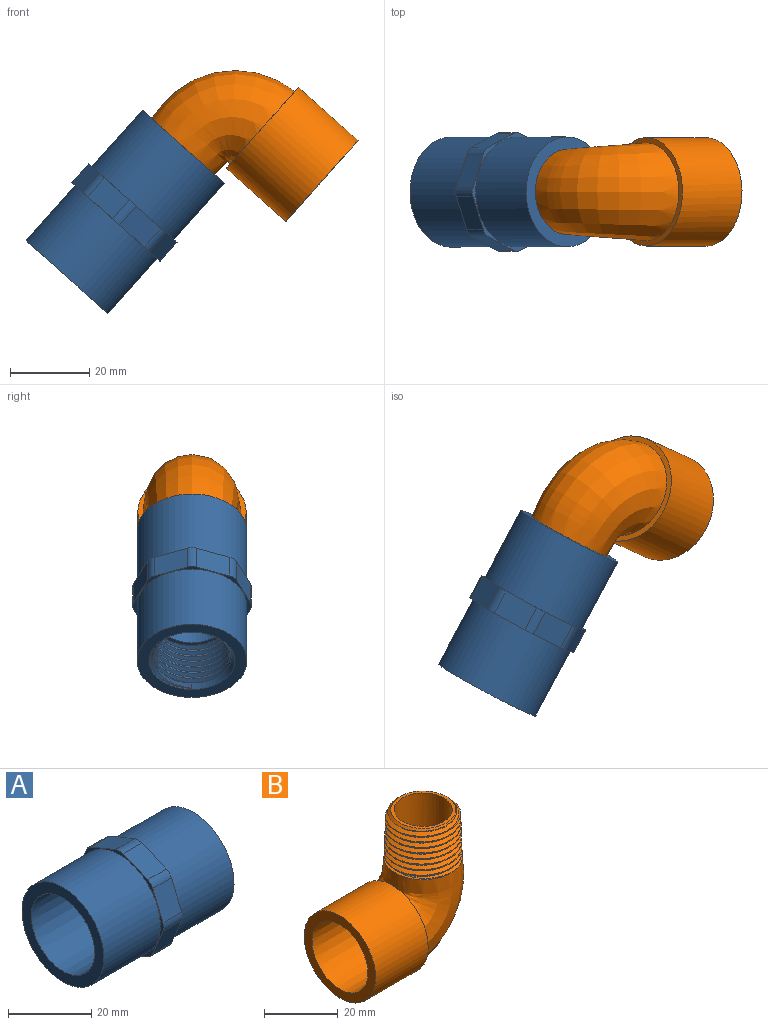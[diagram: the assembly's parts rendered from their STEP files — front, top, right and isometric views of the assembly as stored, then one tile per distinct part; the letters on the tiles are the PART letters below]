
ASSEMBLY  parts=2 mates=1
PART A: 32 faces, bbox 44.5x30.1x30.1 mm
  f0: cylinder r=13.91mm len=27.81mm, axis (1,0,0), area 1675.6mm2, adj f10,f15
  f1: cone r=10.67mm half-angle=1.8deg, axis (1,0,0), area 109.5mm2, adj f3,f4,f5,f9
  f2: cone r=10.89mm half-angle=45deg, axis (1,0,0), area 9.5mm2, adj f3,f4,f6
  f3: cone r=10.89mm half-angle=45deg, axis (1,0,0), area 62.9mm2, adj f1,f2,f5,f6,f7
  f4: bspline ~21.56x21.53mm, area 482.4mm2, adj f1,f2,f6,f9
  f5: bspline ~21.54x21.53mm, area 458mm2, adj f1,f3,f6,f9
  f6: bspline ~19.47x19.44mm, area 213.8mm2, adj f2,f3,f4,f5,f9
  f7: plane 27.81x27.81mm, normal (1,0,0), area 234.7mm2, adj f3,f8
  f8: cylinder r=13.91mm len=27.81mm, axis (1,0,0), area 1631.2mm2, adj f7,f14
  f9: plane 19.52x19.37mm, normal (1,0,0), area 78.8mm2, adj f1,f4,f5,f6,f11
  f10: plane 27.81x27.81mm, normal (-1,0,0), area 243.2mm2, adj f0,f13
  f11: cylinder r=8.33mm len=16.66mm, axis (1,0,0), area 600mm2, adj f9,f12
  f12: plane 21.23x21.23mm, normal (-1,0,0), area 136.1mm2, adj f11,f13
  f13: cone r=10.62mm half-angle=0.5deg, axis (-1,0,0), area 1288.5mm2, adj f10,f12
  f14: plane 30.08x30.08mm, normal (1,0,0), area 52.8mm2, adj f8,f16,f17,f18,f19,f20,f21,f22
  f15: plane 30.08x30.08mm, normal (-1,0,0), area 52.8mm2, adj f0,f16,f17,f18,f19,f20,f21,f22
  f16: cylinder r=3.17mm len=6.35mm, axis (-1,0,0), area 15.8mm2, adj f14,f15,f17,f31
  f17: plane 8.39x6.35mm, normal (0,0.38,0.92), area 57.7mm2, adj f14,f15,f16,f18
  f18: cylinder r=3.17mm len=6.35mm, axis (-1,0,0), area 15.8mm2, adj f14,f15,f17,f19
  f19: plane 8.39x6.35mm, normal (0,-0.38,0.92), area 57.7mm2, adj f14,f15,f18,f20
  f20: cylinder r=3.17mm len=6.35mm, axis (-1,0,0), area 15.8mm2, adj f14,f15,f19,f21
  f21: plane 8.39x6.35mm, normal (0,-0.92,0.38), area 57.7mm2, adj f14,f15,f20,f22
  f22: cylinder r=3.17mm len=6.35mm, axis (-1,0,0), area 15.8mm2, adj f14,f15,f21,f23
  f23: plane 8.39x6.35mm, normal (0,-0.92,-0.38), area 57.7mm2, adj f14,f15,f22,f24
  f24: cylinder r=3.17mm len=6.35mm, axis (-1,0,0), area 15.8mm2, adj f14,f15,f23,f25
  f25: plane 8.39x6.35mm, normal (0,-0.38,-0.92), area 57.7mm2, adj f14,f15,f24,f26
  f26: cylinder r=3.17mm len=6.35mm, axis (-1,0,0), area 15.8mm2, adj f14,f15,f25,f27
  f27: plane 8.39x6.35mm, normal (0,0.38,-0.92), area 57.7mm2, adj f14,f15,f26,f28
  f28: cylinder r=3.17mm len=6.35mm, axis (-1,0,0), area 15.8mm2, adj f14,f15,f27,f29
  f29: plane 8.39x6.35mm, normal (0,0.92,-0.38), area 57.7mm2, adj f14,f15,f28,f30
  f30: cylinder r=3.17mm len=6.35mm, axis (-1,0,0), area 15.8mm2, adj f14,f15,f29,f31
  f31: plane 8.39x6.35mm, normal (0,0.92,0.38), area 57.7mm2, adj f14,f15,f16,f30
PART B: 17 faces, bbox 43.6x28x47.9 mm
  f0: plane 27.44x27.44mm, normal (1,0,0), area 113.2mm2, adj f3,f6
  f1: plane 27.43x27.43mm, normal (-1,0,0), area 226.6mm2, adj f2,f3
  f2: cone r=10.62mm half-angle=0.4deg, axis (-1,0,0), area 1314.1mm2, adj f1,f4
  f3: cylinder r=13.72mm len=27.43mm, axis (-1,0,0), area 1740.2mm2, adj f0,f1
  f4: plane 21.23x21.23mm, normal (-1,0,0), area 158.1mm2, adj f2,f5
  f5: cylinder r=7.9mm len=15.8mm, axis (-1,0,0), area 31.5mm2, adj f4,f16
  f6: bspline ~29.59x24.64mm, area 1723.5mm2, adj f0,f7,f8
  f7: plane 21.94x21.94mm, normal (0,0,1), area 34.8mm2, adj f6,f13,f14,f15
  f8: cone r=10.67mm half-angle=1.8deg, axis (0,0,-1), area 149.9mm2, adj f6,f9,f10,f13,f15
  f9: cone r=8.83mm half-angle=45deg, axis (0,0,-1), area 69.1mm2, adj f8,f10,f11,f13,f14,f15
  f10: cone r=8.83mm half-angle=45deg, axis (0,0,-1), area 0mm2, adj f8,f9,f15
  f11: plane 17.67x17.67mm, normal (0,0,1), area 49.1mm2, adj f9,f12
  f12: cylinder r=7.9mm len=15.8mm, axis (0,0,-1), area 781.6mm2, adj f11,f16
  f13: bspline ~21.6x21.54mm, area 639.3mm2, adj f7,f8,f9,f14
  f14: bspline ~19.17x19.11mm, area 131.1mm2, adj f7,f9,f13,f15
  f15: bspline ~21.65x21.59mm, area 659.4mm2, adj f7,f8,f9,f10,f14
  f16: bspline ~25.17x19.97mm, area 1178.2mm2, adj f5,f12
PLACE A rot(axis=(0,1,0),131.7deg) t=(-11.74,0,-5.74)mm
PLACE B rot(axis=(0,-1,0),138.3deg) t=(19.91,0,29.74)mm
MATE cylindrical B.f8 <-> A.f0  axis (-0.67,0,-0.75) through (-2.07,0,5.1)mm
